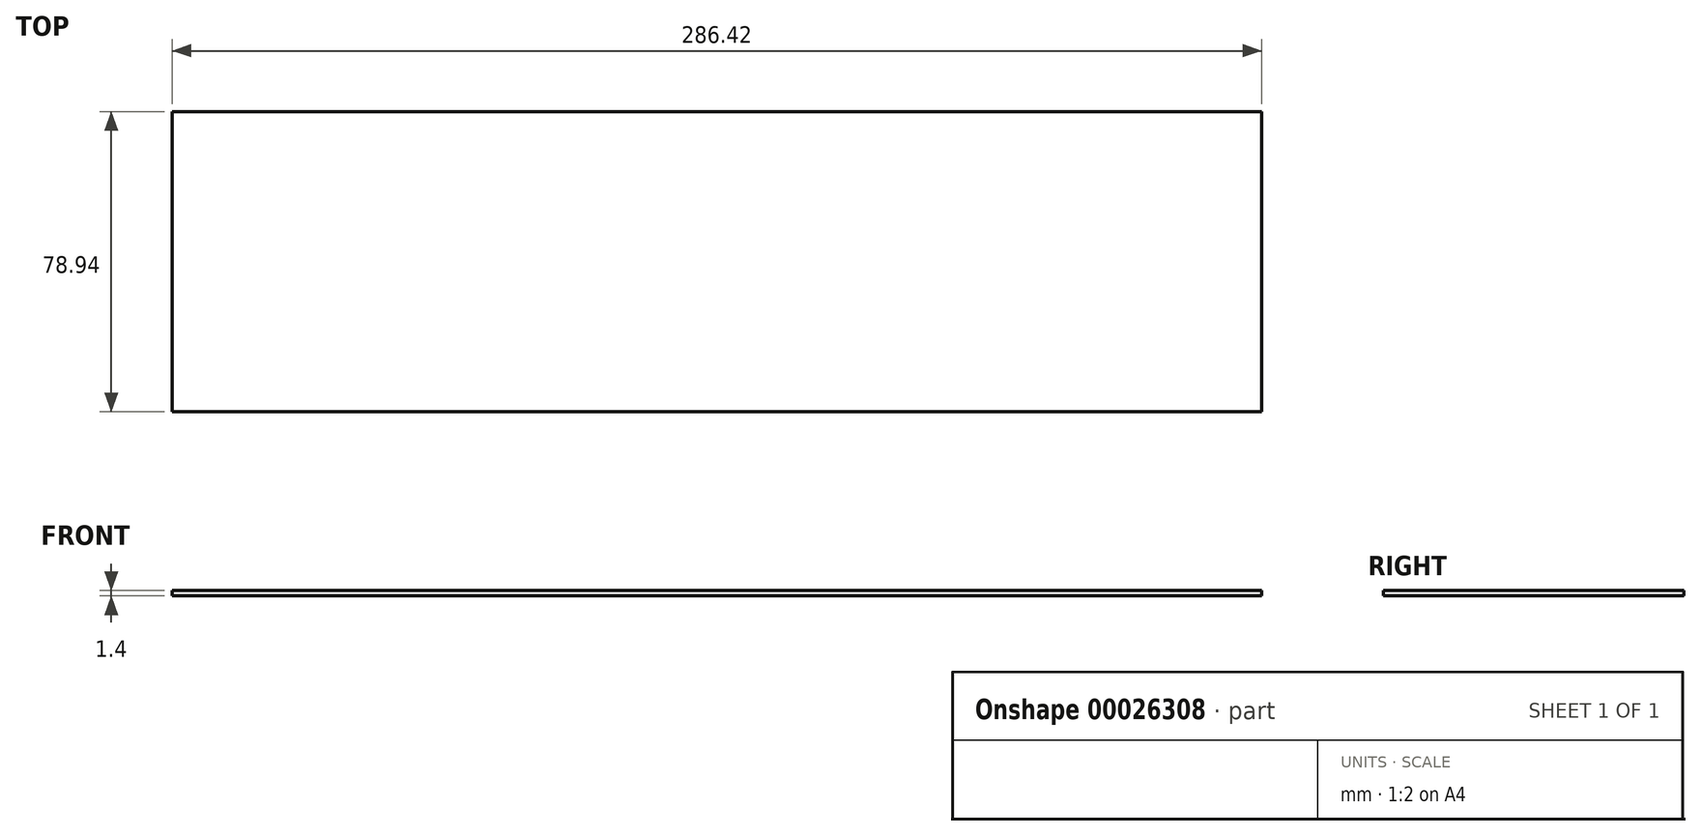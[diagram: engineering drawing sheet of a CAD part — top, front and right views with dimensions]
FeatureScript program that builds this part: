
annotation { "Feature Type Name" : "Feature", "Feature Type Description" : "" }
export const myFeature = defineFeature(function(context is Context, id is Id, definition is map)
    precondition{}
    {
        {
            var Q0;
            Q0=qCreatedBy(makeId("Top.planeOp"),FACE);
            var sketch = newSketch(context, id + "F0", { "sketchPlane" : qUnion([Q0])});
            skLineSegment(sketch, "E0.bottom", {"start": v(-130.03, -26.73) * mm, "end": v(156.4, -26.73) * mm});
            skLineSegment(sketch, "E0.top", {"start": v(-130.03, 52.21) * mm, "end": v(156.4, 52.21) * mm});
            skLineSegment(sketch, "E0.left", {"start": v(-130.03, -26.73) * mm, "end": v(-130.03, 52.21) * mm});
            skLineSegment(sketch, "E0.right", {"start": v(156.4, -26.73) * mm, "end": v(156.4, 52.21) * mm});
            skSolve(sketch);
        }
        {
            var Q0;
            Q0 = qSketchRegion(id + "F0", true);
            var Q1;
            Q1=makeQuery(id+"F0.imprint","IMPRINT",FACE,{"disambiguationData":[TD([[makeQuery(id+"F0.imprint","IMPRINT",EDGE,{"derivedFrom":sQuery(id+"F0.wireOp",EDGE,"E0.bottom")}),1.0]])]});
            extrude(context, id + "F1", {"entities" : qUnion([Q0, Q1]), "depth" : 1.4 * mm});
        }
    });
